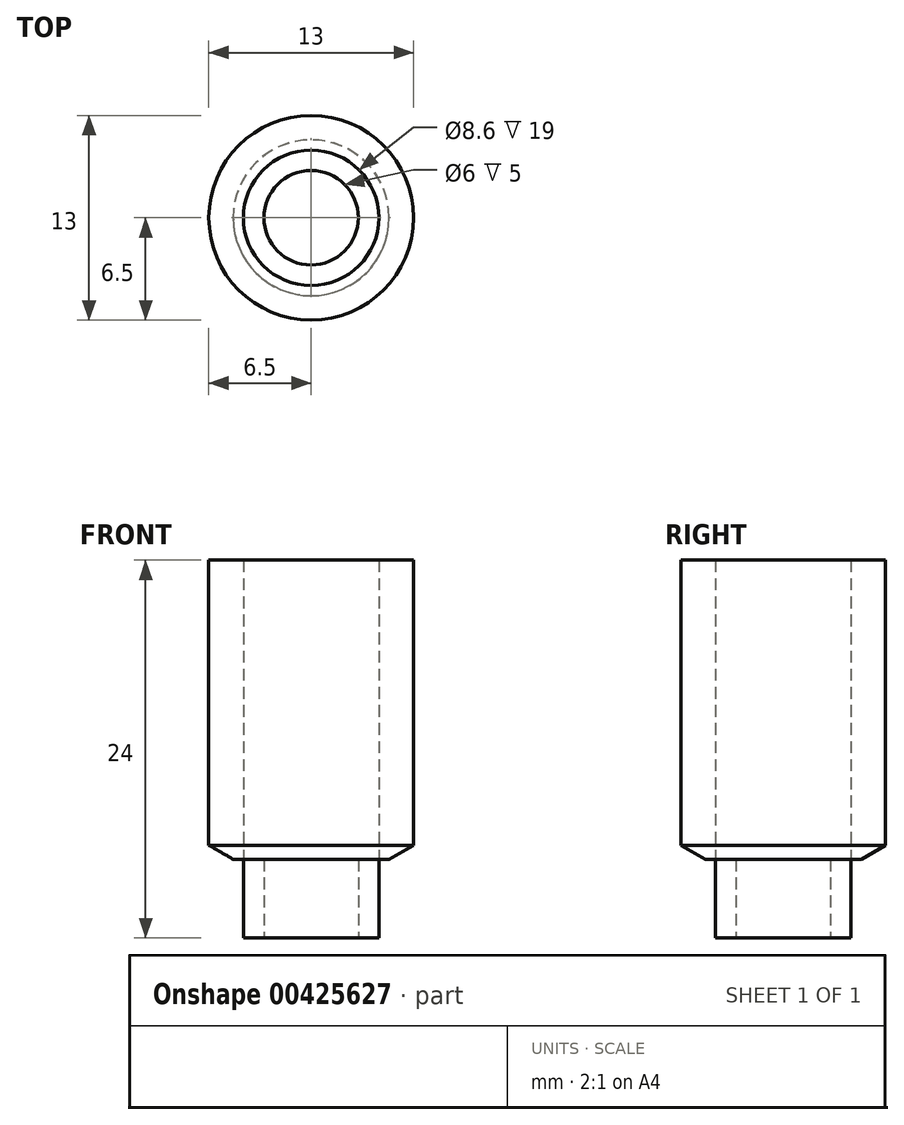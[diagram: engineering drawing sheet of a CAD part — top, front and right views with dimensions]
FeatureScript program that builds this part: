
annotation { "Feature Type Name" : "Feature", "Feature Type Description" : "" }
export const myFeature = defineFeature(function(context is Context, id is Id, definition is map)
    precondition{}
    {
        {
            var Q0;
            Q0=qCreatedBy(makeId("Top.planeOp"),FACE);
            var sketch = newSketch(context, id + "F0", { "sketchPlane" : qUnion([Q0])});
            skCircle(sketch, "E0", {"center": v(0, 0) * mm, "radius": 4.3 * mm});
            skCircle(sketch, "E1", {"center": v(0, 0) * mm, "radius": 3 * mm});
            skSolve(sketch);
        }
        {
            var Q0;
            Q0=makeQuery(id+"F0.imprint","IMPRINT",FACE,{"disambiguationData":[TD([[makeQuery(id+"F0.imprint","IMPRINT",EDGE,{"derivedFrom":sQuery(id+"F0.wireOp",EDGE,"E0")}),1.0]])]});
            extrude(context, id + "F1", {"entities" : qUnion([Q0]), "depth" : 5 * mm});
        }
        {
            var Q0;
            Q0=makeQuery(id+"F1.opExtrude","CAP_FACE",FACE,{"disambiguationData":[OSD([sQuery(id+"F0.wireOp",EDGE,"E0"),sQuery(id+"F0.wireOp",EDGE,"E1")])],"isStart":false});
            var sketch = newSketch(context, id + "F2", { "sketchPlane" : qUnion([Q0])});
            skCircle(sketch, "E2", {"center": v(0, 0) * mm, "radius": 6.5 * mm});
            skSolve(sketch);
        }
        {
            var Q0;
            Q0=makeQuery(id+"F2.imprint","IMPRINT",FACE,{"disambiguationData":[TD([[makeQuery(id+"F2.imprint","IMPRINT",EDGE,{"derivedFrom":sQuery(id+"F2.wireOp",EDGE,"E2")}),1.0]])]});
            extrude(context, id + "F3", {"entities" : qUnion([Q0]), "depth" : 19 * mm});
        }
        {
            var Q0;
            Q0=qCreatedBy(makeId("Front.planeOp"),FACE);
            var sketch = newSketch(context, id + "F4", { "sketchPlane" : qUnion([Q0])});
            skLineSegment(sketch, "E3", {"start": v(6.5, 4.1) * mm, "end": v(6.5, 5.9) * mm});
            skLineSegment(sketch, "E4", {"start": v(6.5, 5.9) * mm, "end": v(4.95, 5) * mm});
            skLineSegment(sketch, "E5", {"start": v(4.95, 5) * mm, "end": v(6.5, 4.1) * mm});
            skSolve(sketch);
        }
        {
            var Q0;
            Q0=makeQuery(id+"F4.imprint","IMPRINT",FACE,{"disambiguationData":[TD([[makeQuery(id+"F4.imprint","IMPRINT",EDGE,{"derivedFrom":sQuery(id+"F4.wireOp",EDGE,"E3")}),1.0]])]});
            var Q1;
            Q1=makeQuery(id+"F3.opExtrude","SWEPT_FACE",FACE,{"disambiguationData":[OSD([sQuery(id+"F2.wireOp",EDGE,"E2")])]});
            revolve(context, id + "F5", {"operationType" : NewBodyOperationType.REMOVE, "entities" : qUnion([Q0]), "axis" : qUnion([Q1]), "revolveType" : RevolveType.FULL, "oppositeDirection" : true});
        }
    });
